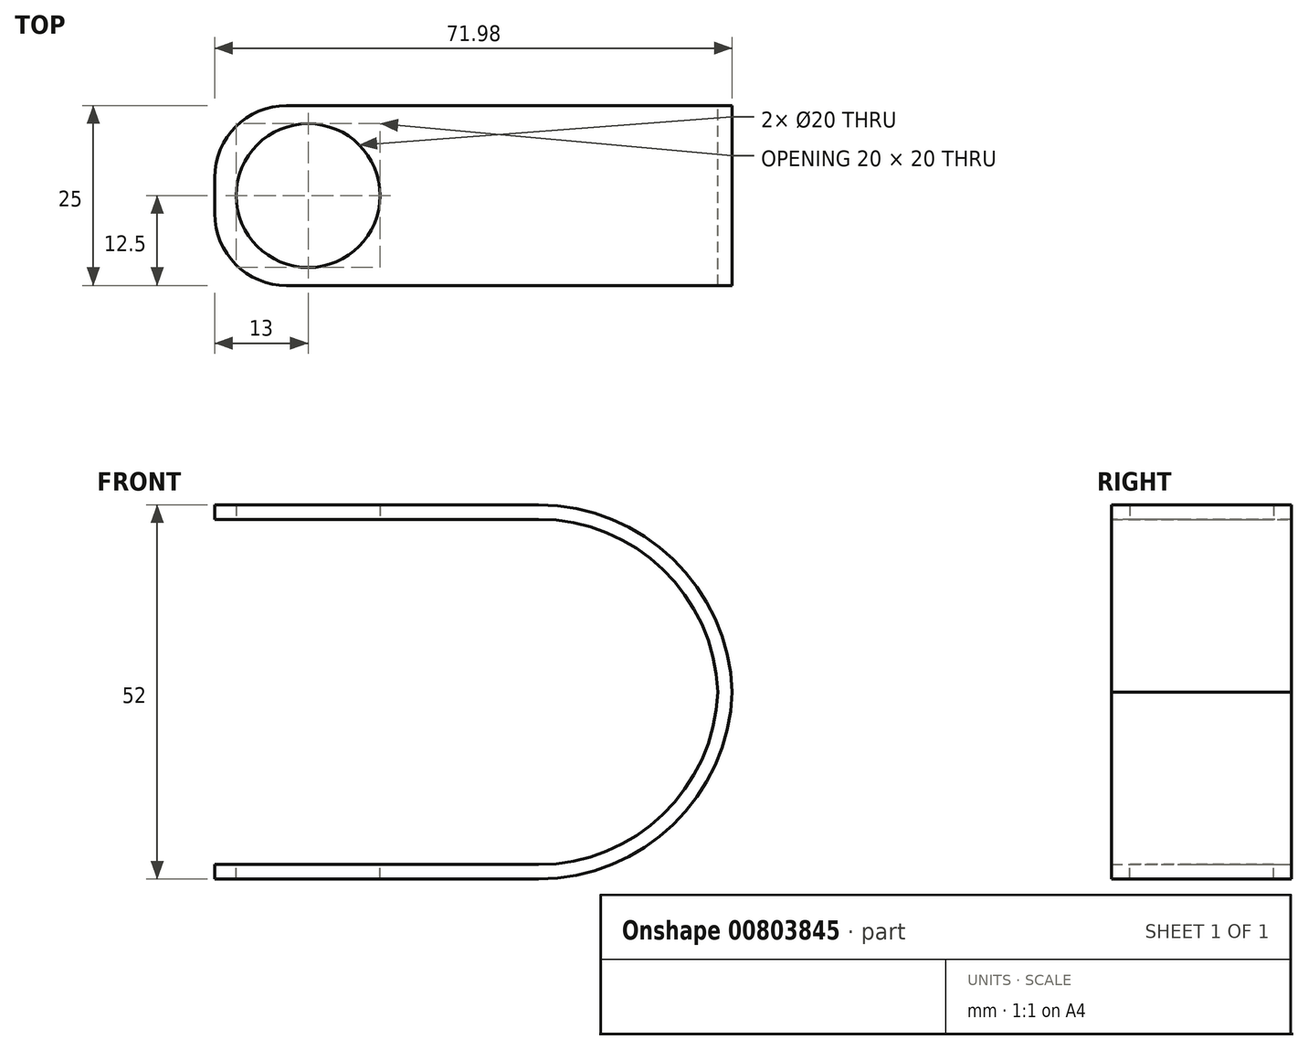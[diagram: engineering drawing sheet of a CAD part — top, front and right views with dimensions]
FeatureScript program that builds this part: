
annotation { "Feature Type Name" : "Feature", "Feature Type Description" : "" }
export const myFeature = defineFeature(function(context is Context, id is Id, definition is map)
    precondition{}
    {
        {
            var Q0;
            Q0=qCreatedBy(makeId("Front.planeOp"),FACE);
            var sketch = newSketch(context, id + "F0", { "sketchPlane" : qUnion([Q0])});
            skLineSegment(sketch, "E0", {"start": v(-45, 24) * mm, "end": v(0, 24) * mm});
            skArc(sketch, "E1", {"start": v(0, 24) * mm, "mid": v(17.32, 17.03) * mm, "end": v(24.98, 0) * mm});
            skLineSegment(sketch, "E2", {"start": v(-45, 24) * mm, "end": v(-45, 26) * mm});
            skLineSegment(sketch, "E3", {"start": v(-45, 26) * mm, "end": v(0, 26) * mm});
            skArc(sketch, "E4", {"start": v(0, 26) * mm, "mid": v(18.73, 18.44) * mm, "end": v(26.98, 0) * mm});
            skLineSegment(sketch, "E5", {"start": v(24.98, 0) * mm, "end": v(26.98, 0) * mm});
            skSolve(sketch);
        }
        {
            var Q0;
            Q0 = qSketchRegion(id + "F0", true);
            extrude(context, id + "F1", {"entities" : qUnion([Q0]), "depth" : 25 * mm, "offsetDistance" : 25 * mm});
        }
        {
            var Q0;
            Q0=makeQuery(id+"F1.opExtrude","SWEPT_FACE",FACE,{"disambiguationData":[OSD([sQuery(id+"F0.wireOp",EDGE,"E0")])]});
            var sketch = newSketch(context, id + "F2", { "sketchPlane" : qUnion([Q0])});
            skCircle(sketch, "E6", {"center": v(-32, 12.5) * mm, "radius": 10 * mm});
            skPoint(sketch, "E6.centerSnap0", {"position": v(-45, 12.5) * mm});
            skSolve(sketch);
        }
        {
            var Q0;
            Q0 = qSketchRegion(id + "F2", true);
            extrude(context, id + "F3", {"entities" : qUnion([Q0]), "operationType" : NewBodyOperationType.REMOVE, "endBound" : BoundingType.THROUGH_ALL, "oppositeDirection" : true, "depth" : 25 * mm, "offsetDistance" : 25 * mm});
        }
        {
            var Q0;
            Q0=makeQuery(id+"F1.opExtrude","SWEPT_BODY",BODY,{"disambiguationData":[OSD([sQuery(id+"F0.wireOp",EDGE,"E0"),sQuery(id+"F0.wireOp",EDGE,"E1"),sQuery(id+"F0.wireOp",EDGE,"E2"),sQuery(id+"F0.wireOp",EDGE,"E3"),sQuery(id+"F0.wireOp",EDGE,"E4"),sQuery(id+"F0.wireOp",EDGE,"E5")])]});
            var Q1;
            Q1=qCreatedBy(makeId("Top.planeOp"),FACE);
            mirror(context, id + "F4", {"operationType" : NewBodyOperationType.ADD, "entities" : qUnion([Q0]), "mirrorPlane" : qUnion([Q1])});
        }
        {
            var Q0;
            Q0=makeQuery(id+"F1.opExtrude","CAP_EDGE",EDGE,{"disambiguationData":[OSD([sQuery(id+"F0.wireOp",EDGE,"E2")])],"isStart":false});
            var Q1;
            Q1=makeQuery(id+"F4.opPattern","COPY",EDGE,{"derivedFrom":makeQuery(id+"F1.opExtrude","CAP_EDGE",EDGE,{"disambiguationData":[OSD([sQuery(id+"F0.wireOp",EDGE,"E2")])],"isStart":false}),"instanceName":"1"});
            var Q2;
            Q2=makeQuery(id+"F4.opPattern","COPY",EDGE,{"derivedFrom":makeQuery(id+"F1.opExtrude","CAP_EDGE",EDGE,{"disambiguationData":[OSD([sQuery(id+"F0.wireOp",EDGE,"E2")])],"isStart":true}),"instanceName":"1"});
            var Q3;
            Q3=makeQuery(id+"F1.opExtrude","CAP_EDGE",EDGE,{"disambiguationData":[OSD([sQuery(id+"F0.wireOp",EDGE,"E2")])],"isStart":true});
            fillet(context, id + "F5", {"entities" : qUnion([Q0, Q1, Q2, Q3]), "radius" : 10 * mm, "tangentPropagation" : true, "allowEdgeOverflow" : false});
        }
    });
